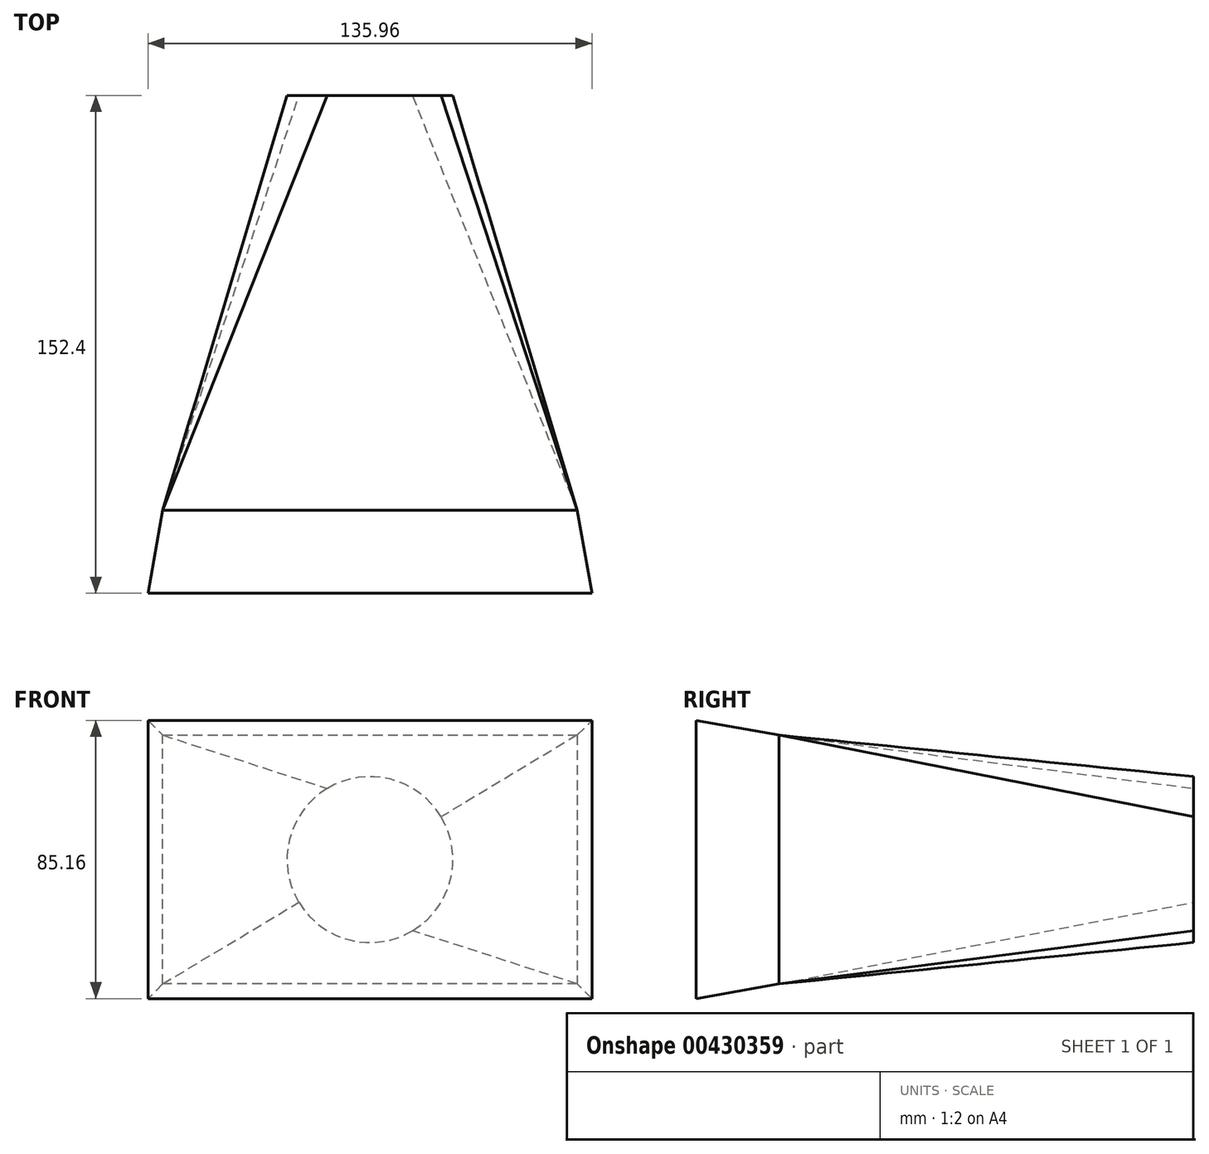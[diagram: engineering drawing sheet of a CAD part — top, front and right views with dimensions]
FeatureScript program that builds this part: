
annotation { "Feature Type Name" : "Feature", "Feature Type Description" : "" }
export const myFeature = defineFeature(function(context is Context, id is Id, definition is map)
    precondition{}
    {
        {
            var Q0;
            Q0=qCreatedBy(makeId("Front.planeOp"),FACE);
            var sketch = newSketch(context, id + "F0", { "sketchPlane" : qUnion([Q0])});
            skLineSegment(sketch, "E0.bottom", {"start": v(63.5, 38.1) * mm, "end": v(-63.5, 38.1) * mm});
            skLineSegment(sketch, "E0.top", {"start": v(63.5, -38.1) * mm, "end": v(-63.5, -38.1) * mm});
            skLineSegment(sketch, "E0.left", {"start": v(63.5, 38.1) * mm, "end": v(63.5, -38.1) * mm});
            skLineSegment(sketch, "E0.right", {"start": v(-63.5, 38.1) * mm, "end": v(-63.5, -38.1) * mm});
            skPoint(sketch, "E0.middle", {"position": v(0, 0) * mm});
            skSolve(sketch);
        }
        {
            var Q0;
            Q0 = qSketchRegion(id + "F0", true);
            extrude(context, id + "F1", {"entities" : qUnion([Q0]), "depth" : 25.4 * mm, "hasDraft" : true, "draftAngle" : 10 * degree});
        }
        {
            var Q0;
            Q0=makeQuery(id+"F1.opExtrude","CAP_FACE",FACE,{"disambiguationData":[OSD([sQuery(id+"F0.wireOp",EDGE,"E0.bottom"),sQuery(id+"F0.wireOp",EDGE,"E0.top"),sQuery(id+"F0.wireOp",EDGE,"E0.left"),sQuery(id+"F0.wireOp",EDGE,"E0.right")])],"isStart":true});
            cPlane(context, id + "F2", {"entities" : qUnion([Q0]), "cplaneType" : CPlaneType.OFFSET, "offset" : 127 * mm, "width" : 152.4 * mm, "height" : 152.4 * mm});
        }
        {
            var Q0;
            Q0=qCreatedBy(id+"F2.planeOp",FACE);
            var sketch = newSketch(context, id + "F3", { "sketchPlane" : qUnion([Q0])});
            skCircle(sketch, "E1", {"center": v(0, 0) * mm, "radius": 25.4 * mm});
            skSolve(sketch);
        }
        {
            var Q1;
            Q1=makeQuery(id+"F1.opExtrude","CAP_FACE",FACE,{"disambiguationData":[OSD([sQuery(id+"F0.wireOp",EDGE,"E0.bottom"),sQuery(id+"F0.wireOp",EDGE,"E0.top"),sQuery(id+"F0.wireOp",EDGE,"E0.left"),sQuery(id+"F0.wireOp",EDGE,"E0.right")])],"isStart":true});
            var Q2;
            Q2=makeQuery(id+"F3.imprint","IMPRINT",FACE,{"disambiguationData":[TD([[makeQuery(id+"F3.imprint","IMPRINT",EDGE,{"derivedFrom":sQuery(id+"F3.wireOp",EDGE,"E1")}),1.0]])]});
            loft(context, id + "F4", {"operationType" : NewBodyOperationType.ADD, "sheetProfilesArray" : [{ "sheetProfileEntities" : qUnion([Q1]) }, { "sheetProfileEntities" : qUnion([Q2]) }]});
        }
    });
